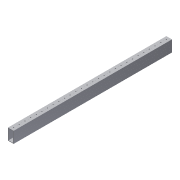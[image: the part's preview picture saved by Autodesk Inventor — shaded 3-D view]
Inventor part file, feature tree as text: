
AUTODESK INVENTOR PART (.ipt)
format: ipt  version: 2015 (Build 190159000, 159)  size: 363,008 bytes
history: native  units: in
note: dims shown in document units (in); Inventor stores cm internally (conversion verified against a paired STEP export)
features: other x3, extrude x3, sketch x3, pattern_linear x1
ambient origin geometry x8: Origin, YZ Plane, XZ Plane, XY Plane, X Axis, Y Axis, Z Axis, Center Point
bodies: Solid1 (feature_tree)
feature tree (10):
  other  "Blocks"
  extrude  "Extrusion1"  Depth=0.05in
  extrude  "Extrusion2"  Depth=0.164in
  pattern_linear  "Rectangular Pattern1"  Spacing1=59.0in  [1 undecoded]
  extrude  "Extrusion3"  Depth=2.0in
  sketch  "Sketch1"  dims[d0=60.0in d1=0.0in d11=0.05in]
  other  "VersaFrameProfile"
  sketch  "Sketch2"  dims[d12=0.164in d13=0.164in]
  sketch  "Sketch3"  dims[d15=1.0in d16=59.0in d17=0.0in d18=11.811in d20=2.0in d21=1.0in d22=2.0in d24=0.0in]
  other  "VersaFrameProfile:1"
note: 1 required parameter value undecoded (feature->parameter linkage not recoverable at this tier; creation-order binding heuristic only, values carry confidence <= 0.55)
